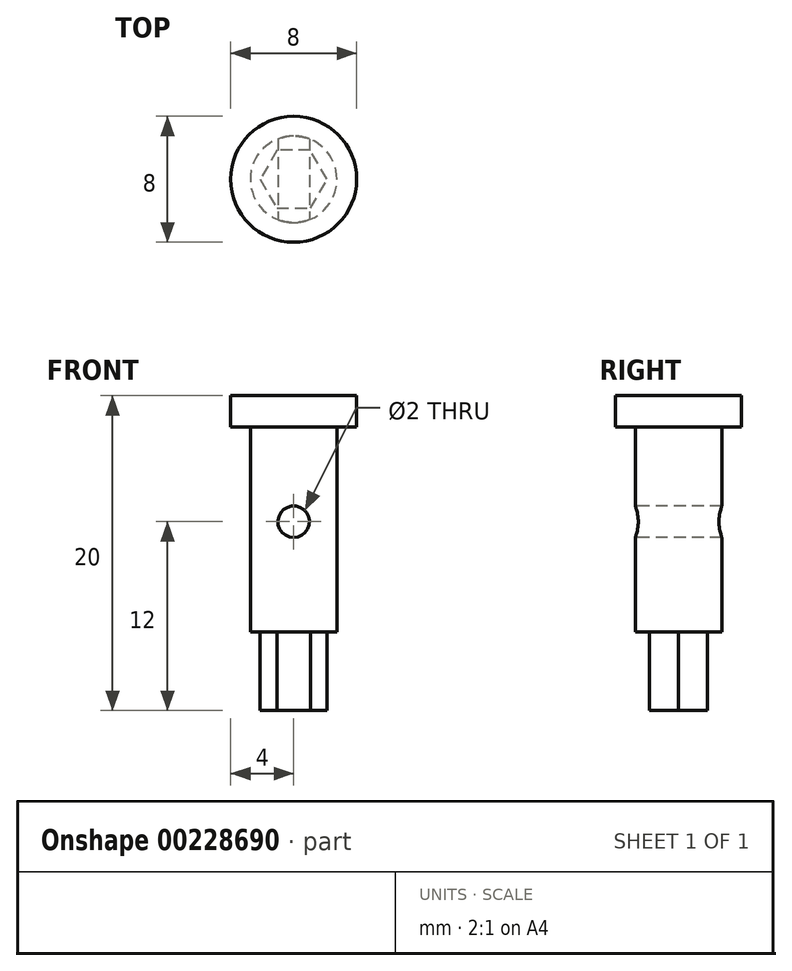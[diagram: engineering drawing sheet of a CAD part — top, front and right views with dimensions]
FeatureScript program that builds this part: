
annotation { "Feature Type Name" : "Feature", "Feature Type Description" : "" }
export const myFeature = defineFeature(function(context is Context, id is Id, definition is map)
    precondition{}
    {
        {
            var Q0;
            Q0=qCreatedBy(makeId("Top.planeOp"),FACE);
            var sketch = newSketch(context, id + "F0", { "sketchPlane" : qUnion([Q0])});
            skCircle(sketch, "E0", {"center": v(0, 0) * mm, "radius": 4 * mm});
            skCircle(sketch, "E1", {"center": v(0, 0) * mm, "radius": 2.75 * mm});
            skSolve(sketch);
        }
        {
            var Q0;
            Q0=makeQuery(id+"F0.imprint","IMPRINT",FACE,{"disambiguationData":[TD([[makeQuery(id+"F0.imprint","IMPRINT",EDGE,{"derivedFrom":sQuery(id+"F0.wireOp",EDGE,"E0")}),1.0]])]});
            var Q1;
            Q1=makeQuery(id+"F0.imprint","IMPRINT",FACE,{"disambiguationData":[TD([[makeQuery(id+"F0.imprint","IMPRINT",EDGE,{"derivedFrom":sQuery(id+"F0.wireOp",EDGE,"E1")}),1.0]])]});
            extrude(context, id + "F1", {"entities" : qUnion([Q0, Q1]), "depth" : 2 * mm});
        }
        {
            var Q0;
            Q0=makeQuery(id+"F0.imprint","IMPRINT",FACE,{"disambiguationData":[TD([[makeQuery(id+"F0.imprint","IMPRINT",EDGE,{"derivedFrom":sQuery(id+"F0.wireOp",EDGE,"E1")}),1.0]])]});
            extrude(context, id + "F2", {"entities" : qUnion([Q0]), "operationType" : NewBodyOperationType.ADD, "oppositeDirection" : true, "depth" : 13 * mm});
        }
        {
            var Q0;
            Q0=makeQuery(id+"F2.opExtrude","CAP_FACE",FACE,{"disambiguationData":[OSD([sQuery(id+"F0.wireOp",EDGE,"E1")])],"isStart":false});
            var sketch = newSketch(context, id + "F3", { "sketchPlane" : qUnion([Q0])});
            skCircle(sketch, "E2", {"center": v(0, 0) * mm, "radius": 2.12 * mm, "construction": true});
            skLineSegment(sketch, "E3.0", {"start": v(2.13, 0) * mm, "end": v(1.06, -1.84) * mm});
            skLineSegment(sketch, "E3.1", {"start": v(1.06, -1.84) * mm, "end": v(-1.06, -1.84) * mm});
            skLineSegment(sketch, "E3.2", {"start": v(-1.06, -1.84) * mm, "end": v(-2.12, 0) * mm});
            skLineSegment(sketch, "E3.3", {"start": v(-2.12, 0) * mm, "end": v(-1.06, 1.84) * mm});
            skLineSegment(sketch, "E3.4", {"start": v(-1.06, 1.84) * mm, "end": v(1.06, 1.84) * mm});
            skLineSegment(sketch, "E3.5", {"start": v(1.06, 1.84) * mm, "end": v(2.12, 0) * mm});
            skSolve(sketch);
        }
        {
            var Q0;
            Q0=makeQuery(id+"F3.imprint","IMPRINT",FACE,{"disambiguationData":[TD([[makeQuery(id+"F3.imprint","IMPRINT",EDGE,{"derivedFrom":sQuery(id+"F3.wireOp",EDGE,"E3.0")}),-1.0]])]});
            extrude(context, id + "F4", {"entities" : qUnion([Q0]), "operationType" : NewBodyOperationType.ADD, "depth" : 5 * mm});
        }
        {
            var Q0;
            Q0=qCreatedBy(makeId("Top.planeOp"),FACE);
            cPlane(context, id + "F5", {"entities" : qUnion([Q0]), "cplaneType" : CPlaneType.OFFSET, "offset" : 6 * mm, "oppositeDirection" : true, "width" : 150 * mm, "height" : 150 * mm});
        }
        {
            var Q0;
            Q0=qCreatedBy(id+"F5.planeOp",FACE);
            var sketch = newSketch(context, id + "F6", { "sketchPlane" : qUnion([Q0])});
            skLineSegment(sketch, "E4", {"start": v(0, 0) * mm, "end": v(0, 9.58) * mm, "construction": true});
            skSolve(sketch);
        }
        {
            var Q0;
            Q0=qCreatedBy(makeId("Front.planeOp"),FACE);
            cPlane(context, id + "F7", {"entities" : qUnion([Q0]), "cplaneType" : CPlaneType.OFFSET, "offset" : 25 * mm, "width" : 150 * mm, "height" : 150 * mm});
        }
        {
            var Q0;
            Q0=qCreatedBy(id+"F7.planeOp",FACE);
            var sketch = newSketch(context, id + "F8", { "sketchPlane" : qUnion([Q0])});
            skCircle(sketch, "E5", {"center": v(0, -6) * mm, "radius": 1 * mm});
            skSolve(sketch);
        }
        {
            var Q0;
            Q0=makeQuery(id+"F8.imprint","IMPRINT",FACE,{"disambiguationData":[TD([[makeQuery(id+"F8.imprint","IMPRINT",EDGE,{"derivedFrom":sQuery(id+"F8.wireOp",EDGE,"E5")}),1.0]])]});
            extrude(context, id + "F9", {"entities" : qUnion([Q0]), "operationType" : NewBodyOperationType.REMOVE, "oppositeDirection" : true, "depth" : 45 * mm});
        }
    });
